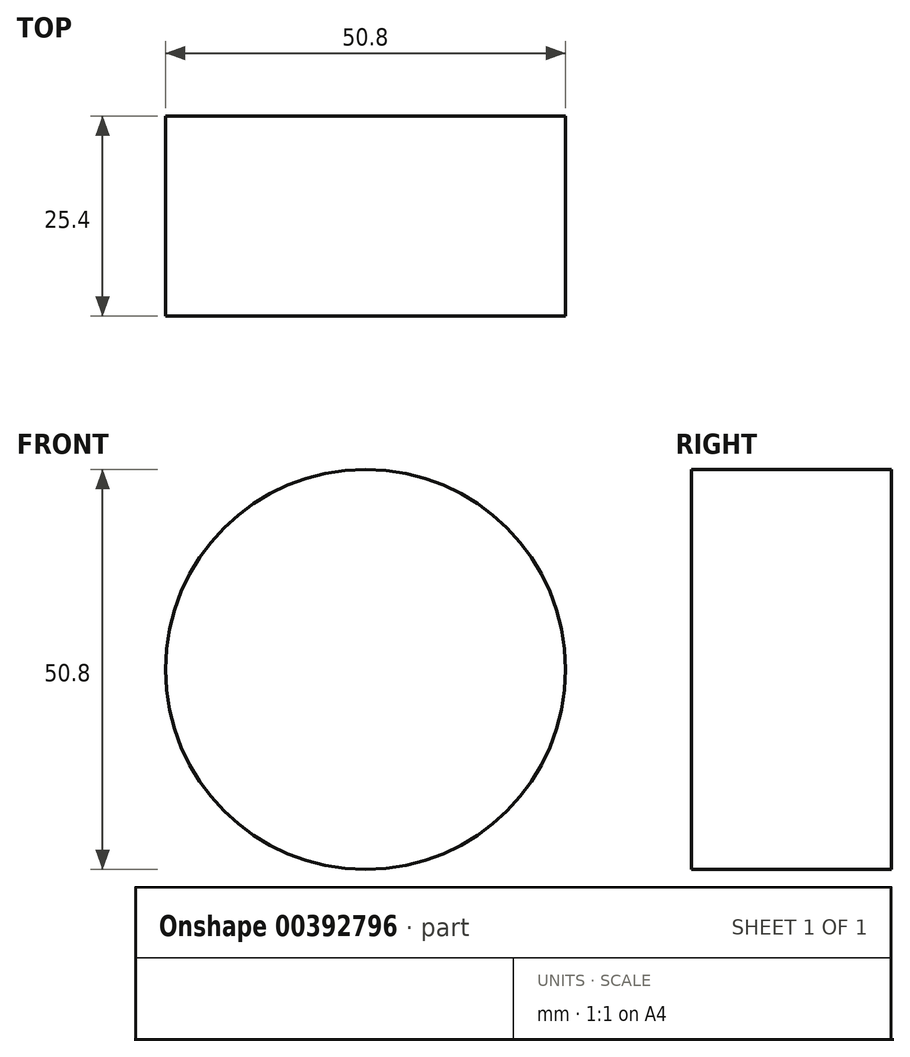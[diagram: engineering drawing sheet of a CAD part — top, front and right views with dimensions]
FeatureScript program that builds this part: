
annotation { "Feature Type Name" : "Feature", "Feature Type Description" : "" }
export const myFeature = defineFeature(function(context is Context, id is Id, definition is map)
    precondition{}
    {
        {
            var Q0;
            Q0=qCreatedBy(makeId("Front.planeOp"),FACE);
            var sketch = newSketch(context, id + "F0", { "sketchPlane" : qUnion([Q0])});
            skCircle(sketch, "E0", {"center": v(0, 0) * mm, "radius": 25.4 * mm});
            skSolve(sketch);
        }
        {
            var Q0;
            Q0=makeQuery(id+"F0.imprint","IMPRINT",FACE,{"disambiguationData":[TD([[makeQuery(id+"F0.imprint","IMPRINT",EDGE,{"derivedFrom":sQuery(id+"F0.wireOp",EDGE,"E0")}),1.0]])]});
            extrude(context, id + "F1", {"entities" : qUnion([Q0]), "depth" : 50.8 * mm});
        }
        {
            var Q0;
            Q0=makeQuery(id+"F1.opExtrude","CAP_FACE",FACE,{"disambiguationData":[OSD([sQuery(id+"F0.wireOp",EDGE,"E0")])],"isStart":true});
            extrude(context, id + "F2", {"entities" : qUnion([Q0]), "operationType" : NewBodyOperationType.REMOVE, "oppositeDirection" : true, "depth" : 25.4 * mm});
        }
    });
